# Revit family: Shower-Valves_and_Controls-KOHLER-Kohler-K-880M_1
name_source: partatom
category: Plumbing Fixtures
units: mm (PartAtom-declared; Revit-internal decimal feet)

## family parameters
Cut with Voids When Loaded = Yes
Host = Face
OmniClass Number = 23.27.31.00
OmniClass Title = Valves
Part Type = Normal
Room Calculation Point = No
Round Connector Dimension = Use Diameter
Shared = No

## types (2) — shared parameters
ADA Compliant = No
Assembly Code = D2020
CW Connection = Yes
Cold Water Inlet = Cold Water Inlet
Date Modified = 01/18/2023
Default Elevation = 36"
Description = 40mm Shower Valve
Drain Included = No
Flow Rate = 40 GPM
HW Connection = Yes
Height = 6 5/16"
Hot Water Inlet = Hot Water Inlet
Length = 5 3/8"
Manufacturer = Kohler Co.
Master Format 2014 = 23 09 13.33
Master Format 2014 Name = Control Valves
Material = Premium Metal Construction
Pressure = 60.00 psi
Product Documentation Link = http://resources.kohler.com
Product Name = Kohler
Tempered Water Outlet = Tempered Water Outlet
URL = https://la.kohler.com
Vent Connection = No
Waste Connection = No
Waste Water Outlet = Waste Water Outlet
WaterSense Certified = No
Width = 3 1/2"

## per-type parameters (varying)
| type | Finish | Model | Product Page URL | Type |
| CP-Polished Chrome | Kohler-Metal-CP-Polished_Chrome | K-880M-CP | https://la.kohler.com | 1 |
| RGD-Polished Rose Gold | Kohler-Metal-RGD-Polished_Rose_Gold | K-880M-RGD |  | 2 |

## geometry (parser evidence)
native form markers: Sweep x4
no freeform markers — native parametric forms only
